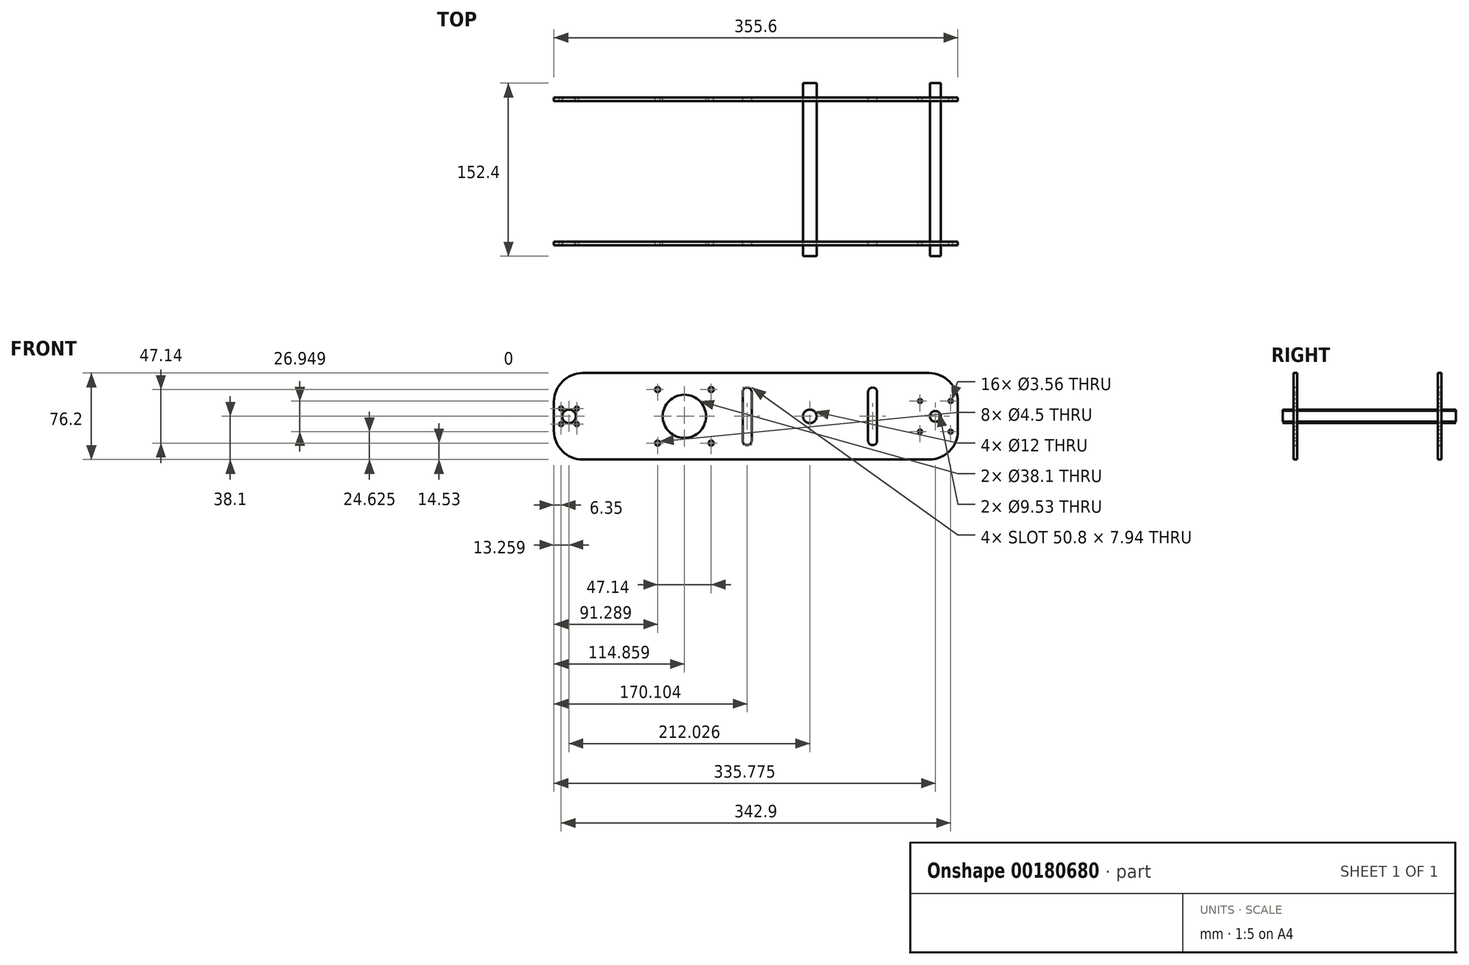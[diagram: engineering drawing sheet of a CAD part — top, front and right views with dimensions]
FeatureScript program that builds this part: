
annotation { "Feature Type Name" : "Feature", "Feature Type Description" : "" }
export const myFeature = defineFeature(function(context is Context, id is Id, definition is map)
    precondition{}
    {
        {
            var Q0;
            Q0=qCreatedBy(makeId("Front.planeOp"),FACE);
            var sketch = newSketch(context, id + "F0", { "sketchPlane" : qUnion([Q0])});
            skLineSegment(sketch, "E0.bottom", {"start": v(152.4, 38.1) * mm, "end": v(-152.4, 38.1) * mm});
            skLineSegment(sketch, "E0.top", {"start": v(152.4, -38.1) * mm, "end": v(-152.4, -38.1) * mm});
            skLineSegment(sketch, "E0.left", {"start": v(177.8, 12.7) * mm, "end": v(177.8, -12.7) * mm});
            skLineSegment(sketch, "E0.right", {"start": v(-177.8, 12.7) * mm, "end": v(-177.8, -12.7) * mm});
            skPoint(sketch, "E0.middle", {"position": v(0, 0) * mm});
            skCircle(sketch, "E1", {"center": v(-164.54, 0) * mm, "radius": 6 * mm});
            skCircle(sketch, "E2", {"center": v(-171.45, 6.9) * mm, "radius": 1.78 * mm});
            skCircle(sketch, "E3.0.1.0", {"center": v(-171.45, -6.9) * mm, "radius": 1.78 * mm});
            skCircle(sketch, "E3.1.0.0", {"center": v(-157.63, 6.9) * mm, "radius": 1.78 * mm});
            skCircle(sketch, "E3.1.1.0", {"center": v(-157.63, -6.9) * mm, "radius": 1.78 * mm});
            skLineSegment(sketch, "E3.direction1", {"start": v(-171.45, 6.9) * mm, "end": v(-157.63, 6.9) * mm, "construction": true});
            skLineSegment(sketch, "E3.direction2", {"start": v(-171.45, 6.9) * mm, "end": v(-171.45, -6.9) * mm, "construction": true});
            skCircle(sketch, "E4", {"center": v(-62.94, 0) * mm, "radius": 19.05 * mm});
            skCircle(sketch, "E5", {"center": v(-86.51, 23.57) * mm, "radius": 2.25 * mm});
            skCircle(sketch, "E6.0.1.0", {"center": v(-86.51, -23.57) * mm, "radius": 2.25 * mm});
            skCircle(sketch, "E6.1.0.0", {"center": v(-39.37, 23.57) * mm, "radius": 2.25 * mm});
            skCircle(sketch, "E6.1.1.0", {"center": v(-39.37, -23.57) * mm, "radius": 2.25 * mm});
            skLineSegment(sketch, "E6.direction1", {"start": v(-86.51, 23.57) * mm, "end": v(-39.37, 23.57) * mm, "construction": true});
            skLineSegment(sketch, "E6.direction2", {"start": v(-86.51, 23.57) * mm, "end": v(-86.51, -23.57) * mm, "construction": true});
            skCircle(sketch, "E7", {"center": v(47.49, 0) * mm, "radius": 6 * mm});
            skCircle(sketch, "E8", {"center": v(157.98, 0) * mm, "radius": 4.76 * mm});
            skCircle(sketch, "E9", {"center": v(144.5, 13.47) * mm, "radius": 1.78 * mm});
            skCircle(sketch, "E10.0.1.0", {"center": v(144.5, -13.47) * mm, "radius": 1.78 * mm});
            skCircle(sketch, "E10.1.0.0", {"center": v(171.45, 13.47) * mm, "radius": 1.78 * mm});
            skCircle(sketch, "E10.1.1.0", {"center": v(171.45, -13.47) * mm, "radius": 1.78 * mm});
            skLineSegment(sketch, "E10.direction1", {"start": v(144.5, 13.47) * mm, "end": v(171.45, 13.47) * mm, "construction": true});
            skLineSegment(sketch, "E10.direction2", {"start": v(144.5, 13.47) * mm, "end": v(144.5, -13.47) * mm, "construction": true});
            skLineSegment(sketch, "E11.bottom", {"start": v(-7.7, -25.4) * mm, "end": v(-7.7, -25.4) * mm});
            skLineSegment(sketch, "E11.top", {"start": v(-7.7, 25.4) * mm, "end": v(-7.7, 25.4) * mm});
            skLineSegment(sketch, "E11.left", {"start": v(-3.73, -21.43) * mm, "end": v(-3.73, 21.43) * mm});
            skLineSegment(sketch, "E11.right", {"start": v(-11.66, -21.43) * mm, "end": v(-11.66, 21.43) * mm});
            skPoint(sketch, "E11.middle", {"position": v(-7.7, 0) * mm});
            skLineSegment(sketch, "E12.bottom", {"start": v(78.99, -25.4) * mm, "end": v(78.99, -25.4) * mm});
            skLineSegment(sketch, "E12.top", {"start": v(78.99, 25.4) * mm, "end": v(78.99, 25.4) * mm});
            skLineSegment(sketch, "E12.left", {"start": v(106.7, -21.43) * mm, "end": v(106.7, 21.43) * mm});
            skLineSegment(sketch, "E12.right", {"start": v(98.76, -21.43) * mm, "end": v(98.76, 21.43) * mm});
            skPoint(sketch, "E12.middle", {"position": v(102.73, 0) * mm});
            skPoint(sketch, "E13.visualSharp", {"position": v(-11.66, -25.4) * mm});
            skArc(sketch, "E13.filletArc", {"start": v(-11.66, -21.43) * mm, "mid": v(-10.5, -24.24) * mm, "end": v(-7.7, -25.4) * mm});
            skPoint(sketch, "E14.visualSharp", {"position": v(-3.73, -25.4) * mm});
            skArc(sketch, "E14.filletArc", {"start": v(-7.7, -25.4) * mm, "mid": v(-4.89, -24.24) * mm, "end": v(-3.73, -21.43) * mm});
            skPoint(sketch, "E15.visualSharp", {"position": v(-11.66, 25.4) * mm});
            skArc(sketch, "E15.filletArc", {"start": v(-7.7, 25.4) * mm, "mid": v(-10.5, 24.24) * mm, "end": v(-11.66, 21.43) * mm});
            skPoint(sketch, "E16.visualSharp", {"position": v(-3.73, 25.4) * mm});
            skArc(sketch, "E16.filletArc", {"start": v(-3.73, 21.43) * mm, "mid": v(-4.89, 24.24) * mm, "end": v(-7.7, 25.4) * mm});
            skPoint(sketch, "E17.visualSharp", {"position": v(98.76, -25.4) * mm});
            skArc(sketch, "E17.filletArc", {"start": v(98.76, -21.43) * mm, "mid": v(99.92, -24.24) * mm, "end": v(102.73, -25.4) * mm});
            skPoint(sketch, "E18.visualSharp", {"position": v(106.7, -25.4) * mm});
            skArc(sketch, "E18.filletArc", {"start": v(102.73, -25.4) * mm, "mid": v(105.54, -24.24) * mm, "end": v(106.7, -21.43) * mm});
            skPoint(sketch, "E19.visualSharp", {"position": v(98.76, 25.4) * mm});
            skArc(sketch, "E19.filletArc", {"start": v(102.73, 25.4) * mm, "mid": v(99.92, 24.24) * mm, "end": v(98.76, 21.43) * mm});
            skPoint(sketch, "E20.visualSharp", {"position": v(106.7, 25.4) * mm});
            skArc(sketch, "E20.filletArc", {"start": v(106.7, 21.43) * mm, "mid": v(105.54, 24.24) * mm, "end": v(102.73, 25.4) * mm});
            skPoint(sketch, "E21.visualSharp", {"position": v(-177.8, 38.1) * mm});
            skArc(sketch, "E21.filletArc", {"start": v(-152.4, 38.1) * mm, "mid": v(-170.36, 30.66) * mm, "end": v(-177.8, 12.7) * mm});
            skPoint(sketch, "E22.visualSharp", {"position": v(-177.8, -38.1) * mm});
            skArc(sketch, "E22.filletArc", {"start": v(-177.8, -12.7) * mm, "mid": v(-170.36, -30.66) * mm, "end": v(-152.4, -38.1) * mm});
            skPoint(sketch, "E23.visualSharp", {"position": v(177.8, 38.1) * mm});
            skArc(sketch, "E23.filletArc", {"start": v(177.8, 12.7) * mm, "mid": v(170.36, 30.66) * mm, "end": v(152.4, 38.1) * mm});
            skPoint(sketch, "E24.visualSharp", {"position": v(177.8, -38.1) * mm});
            skArc(sketch, "E24.filletArc", {"start": v(152.4, -38.1) * mm, "mid": v(170.36, -30.66) * mm, "end": v(177.8, -12.7) * mm});
            skSolve(sketch);
        }
        {
            var Q0;
            Q0=makeQuery(id+"F0.imprint","IMPRINT",FACE,{"disambiguationData":[TD([[makeQuery(id+"F0.imprint","IMPRINT",EDGE,{"derivedFrom":sQuery(id+"F0.wireOp",EDGE,"E0.bottom")}),1.0]])]});
            extrude(context, id + "F1", {"entities" : qUnion([Q0]), "depth" : 3.17 * mm});
        }
        {
            var Q0;
            Q0=makeQuery(id+"F1.opExtrude","SWEPT_BODY",BODY,{"disambiguationData":[OSD([sQuery(id+"F0.wireOp",EDGE,"E0.bottom"),sQuery(id+"F0.wireOp",EDGE,"E0.top"),sQuery(id+"F0.wireOp",EDGE,"E0.left"),sQuery(id+"F0.wireOp",EDGE,"E0.right"),sQuery(id+"F0.wireOp",EDGE,"E1"),sQuery(id+"F0.wireOp",EDGE,"E2"),sQuery(id+"F0.wireOp",EDGE,"E3.0.1.0"),sQuery(id+"F0.wireOp",EDGE,"E3.1.0.0"),sQuery(id+"F0.wireOp",EDGE,"E3.1.1.0"),sQuery(id+"F0.wireOp",EDGE,"E4"),sQuery(id+"F0.wireOp",EDGE,"E5"),sQuery(id+"F0.wireOp",EDGE,"E6.0.1.0"),sQuery(id+"F0.wireOp",EDGE,"E6.1.0.0"),sQuery(id+"F0.wireOp",EDGE,"E6.1.1.0"),sQuery(id+"F0.wireOp",EDGE,"E7"),sQuery(id+"F0.wireOp",EDGE,"E8"),sQuery(id+"F0.wireOp",EDGE,"E9"),sQuery(id+"F0.wireOp",EDGE,"E10.0.1.0"),sQuery(id+"F0.wireOp",EDGE,"E10.1.0.0"),sQuery(id+"F0.wireOp",EDGE,"E10.1.1.0"),sQuery(id+"F0.wireOp",EDGE,"E11.left"),sQuery(id+"F0.wireOp",EDGE,"E11.right"),sQuery(id+"F0.wireOp",EDGE,"E12.left"),sQuery(id+"F0.wireOp",EDGE,"E12.right"),sQuery(id+"F0.wireOp",EDGE,"E13.filletArc"),sQuery(id+"F0.wireOp",EDGE,"E14.filletArc"),sQuery(id+"F0.wireOp",EDGE,"E15.filletArc"),sQuery(id+"F0.wireOp",EDGE,"E16.filletArc"),sQuery(id+"F0.wireOp",EDGE,"E17.filletArc"),sQuery(id+"F0.wireOp",EDGE,"E18.filletArc"),sQuery(id+"F0.wireOp",EDGE,"E19.filletArc"),sQuery(id+"F0.wireOp",EDGE,"E20.filletArc"),sQuery(id+"F0.wireOp",EDGE,"E21.filletArc"),sQuery(id+"F0.wireOp",EDGE,"E22.filletArc"),sQuery(id+"F0.wireOp",EDGE,"E23.filletArc"),sQuery(id+"F0.wireOp",EDGE,"E24.filletArc")])]});
            transform(context, id + "F2", {"entities" : qUnion([Q0]), "transformType" : TransformType.TRANSLATION_3D, "dx" : 0 * mm, "dy" : -127 * mm, "dz" : 0 * mm, "makeCopy" : true});
        }
        {
            var Q0;
            Q0=makeQuery(id+"F0.imprint","IMPRINT",FACE,{"disambiguationData":[TD([[makeQuery(id+"F0.imprint","IMPRINT",EDGE,{"derivedFrom":sQuery(id+"F0.wireOp",EDGE,"E7")}),1.0]])]});
            extrude(context, id + "F3", {"entities" : qUnion([Q0]), "depth" : 139.7 * mm, "hasSecondDirection" : true, "secondDirectionOppositeDirection" : true, "secondDirectionDepth" : 12.7 * mm});
        }
        {
            var Q0;
            Q0=makeQuery(id+"F0.imprint","IMPRINT",FACE,{"disambiguationData":[TD([[makeQuery(id+"F0.imprint","IMPRINT",EDGE,{"derivedFrom":sQuery(id+"F0.wireOp",EDGE,"E8")}),1.0]])]});
            extrude(context, id + "F4", {"entities" : qUnion([Q0]), "depth" : 139.7 * mm, "hasSecondDirection" : true, "secondDirectionOppositeDirection" : true, "secondDirectionDepth" : 12.7 * mm});
        }
    });
